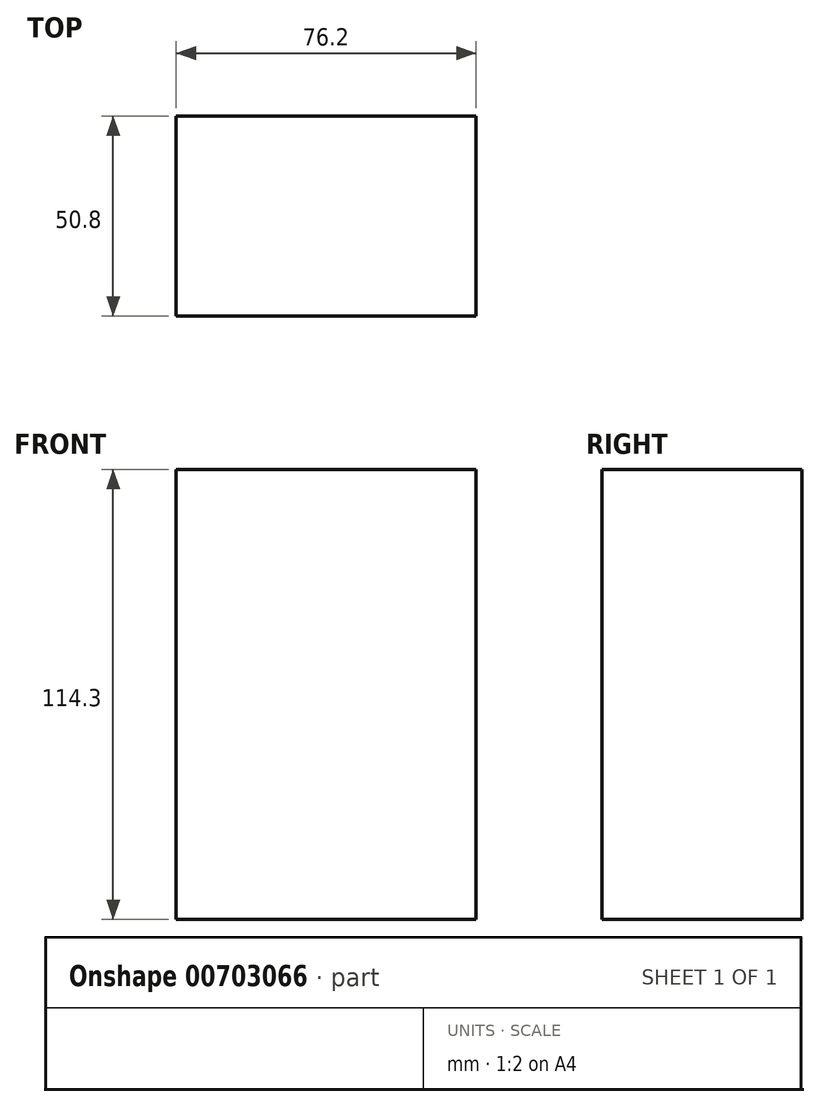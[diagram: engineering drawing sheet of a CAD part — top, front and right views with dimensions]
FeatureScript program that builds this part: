
annotation { "Feature Type Name" : "Feature", "Feature Type Description" : "" }
export const myFeature = defineFeature(function(context is Context, id is Id, definition is map)
    precondition{}
    {
        {
            var Q0;
            Q0=qCreatedBy(makeId("Top.planeOp"),FACE);
            var sketch = newSketch(context, id + "F0", { "sketchPlane" : qUnion([Q0])});
            skLineSegment(sketch, "E0.bottom", {"start": v(-37.16, 25.04) * mm, "end": v(39.04, 25.04) * mm});
            skLineSegment(sketch, "E0.top", {"start": v(-37.16, -25.76) * mm, "end": v(39.04, -25.76) * mm});
            skLineSegment(sketch, "E0.left", {"start": v(-37.16, 25.04) * mm, "end": v(-37.16, -25.76) * mm});
            skLineSegment(sketch, "E0.right", {"start": v(39.04, 25.04) * mm, "end": v(39.04, -25.76) * mm});
            skSolve(sketch);
        }
        {
            var Q0;
            Q0=makeQuery(id+"F0.imprint","IMPRINT",FACE,{"disambiguationData":[TD([[makeQuery(id+"F0.imprint","IMPRINT",EDGE,{"derivedFrom":sQuery(id+"F0.wireOp",EDGE,"E0.bottom")}),-1.0]])]});
            extrude(context, id + "F1", {"entities" : qUnion([Q0]), "depth" : 114.3 * mm, "offsetDistance" : 25.4 * mm});
        }
    });
